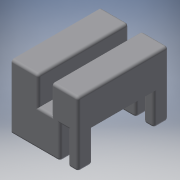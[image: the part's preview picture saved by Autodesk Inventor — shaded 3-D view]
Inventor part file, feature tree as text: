
AUTODESK INVENTOR PART (.ipt)
format: ipt  version: 2018 (Build 220112000, 112)  size: 509,952 bytes
history: native  units: in
note: dims shown in document units (in); Inventor stores cm internally (conversion verified against a paired STEP export)
features: extrude x23, sketch x23, fillet x13, other x4, reference x3, plane x2, projected_geometry x2
ambient origin geometry x8: Origin, YZ Plane, XZ Plane, XY Plane, X Axis, Y Axis, Z Axis, Center Point
bodies: Solid1 (feature_tree)
feature tree (70):
  extrude  "Extrusion1"  Depth=1.0in
  extrude  "Extrusion2"  Depth=0.95in TaperAngle=0.0deg
  extrude  "Extrusion3"  Depth=0.15in
  extrude  "Extrusion4"  Depth=0.15in
  extrude  "Extrusion5"  Depth=0.15in
  extrude  "Extrusion6"  Depth=0.2in TaperAngle=0.0deg
  extrude  "Extrusion7"  Depth=0.125in TaperAngle=0.0deg
  fillet  "Fillet1"  Radius=0.125in
  extrude  "Extrusion8"  Depth=0.03in TaperAngle=0.0deg
  plane  "Work Plane1"
  extrude  "Extrusion10"  Depth=0.03in TaperAngle=0.0deg
  extrude  "Extrusion11"  Depth=1.0in TaperAngle=0.0deg
  extrude  "Extrusion12"  Depth=1.0in TaperAngle=0.0deg
  extrude  "Extrusion13"  Depth=1.0in TaperAngle=0.0deg
  extrude  "Extrusion14"  Depth=1.0in
  extrude  "Extrusion15"  Depth=2.0in TaperAngle=0.0deg
  extrude  "Extrusion16"  Depth=0.07in TaperAngle=0.0deg
  extrude  "Extrusion17"  Depth=0.2in
  extrude  "Extrusion18"  Depth=12323.0in TaperAngle=0.0deg
  extrude  "Extrusion19"  Depth=0.0394in
  extrude  "Extrusion20"  Depth=0.0394in
  extrude  "Extrusion21"  Depth=0.0394in
  sketch  "Sketch24"  dims[d79=0.0394in d80=0.0394in]
  plane  "Work Plane2"
  extrude  "Extrusion22"  Depth=0.0394in
  extrude  "Extrusion24"  Depth=0.0394in
  fillet  "Fillet3"  Radius=0.0394in
  fillet  "Fillet4"  Radius=0.0394in
  fillet  "Fillet5"  Radius=3.0in
  fillet  "Fillet6"  Radius=0.0394in
  fillet  "Fillet7"  [1 undecoded]
  fillet  "Fillet8"  [1 undecoded]
  fillet  "Fillet9"  [1 undecoded]
  fillet  "Fillet10"  [1 undecoded]
  fillet  "Fillet11"  [1 undecoded]
  fillet  "Fillet12"  [1 undecoded]
  fillet  "Fillet13"  [1 undecoded]
  extrude  "Extrusion25"  [1 undecoded]
  fillet  "Fillet14"  [1 undecoded]
  sketch  "Sketch1"  dims[d0=1.0in d1=1.0in]
  sketch  "Sketch2"  dims[d2=1.0in d3=0.0in d7=0.95in d8=0.0in]
  sketch  "Sketch3"  dims[d9=0.15in d10=0.105in]
  sketch  "Sketch4"  dims[d11=1.075in d12=0.0in d13=0.15in]
  sketch  "Sketch5"  dims[d14=1.075in d15=0.0in d16=0.15in]
  sketch  "Sketch6"  dims[d17=0.2in d18=0.0in d19=0.2in d20=0.0in]
  sketch  "Sketch7"  dims[d21=0.19in d22=0.2625in d23=0.0in d24=0.125in]
  sketch  "Sketch8"  dims[d25=0.01in d26=0.0in d29=0.03in d30=0.0in]
  sketch  "Sketch11"  dims[d31=0.03in d32=0.0in d33=0.03in d34=0.0in]
  sketch  "Sketch12"  dims[d35=0.2175in d36=0.0in d37=1.0in d38=0.0in]
  sketch  "Sketch13"  dims[d39=1.0in d40=0.0in d41=1.0in d42=0.0in]
  sketch  "Sketch14"  dims[d43=1.0in d44=0.0in d45=1.0in d46=0.0in]
  sketch  "Sketch15"  dims[d47=1.0in d48=0.0in d49=0.0098in]
  sketch  "Sketch17"  dims[d50=0.0098in d51=2.0in d52=0.0in]
  projected_geometry  "Projected Loop1"
  sketch  "Sketch18"  dims[d53=0.07in d54=0.0in d55=0.07in d56=0.0in]
  sketch  "Sketch19"  dims[d67=0.1in d68=0.2in]
  reference  "Reference1"
  sketch  "Sketch20"  dims[d69=0.4in d70=12323.0in d71=0.0in]
  sketch  "Sketch21"  dims[d73=0.0394in d74=0.0394in]
  sketch  "Sketch22"  dims[d75=0.0394in d76=0.0394in]
  reference  "Reference2"
  sketch  "Sketch23"  dims[d77=0.0394in d78=0.0394in]
  projected_geometry  "Projected Loop2"
  reference  "Reference3"
  sketch  "Sketch27"  dims[d81=0.0394in d82=0.0394in d83=0.0394in d84=0.0394in d85=3.0in d86=0.0in d87=0.0394in]
  sketch  "Sketch28"
  parser-record x1  (decoder bookkeeping rows leaked as tree rows — omitted from the tree; the rows remain in map.json)
  other  "AssemblyNEWarm.iam"
  other  "servo (2):1"
  other  "servo (2):2"
note: 9 required parameter values undecoded (feature->parameter linkage not recoverable at this tier; creation-order binding heuristic only, values carry confidence <= 0.55)
note: 1 file-system path scrubbed to <path> (originals preserved in map.json)
